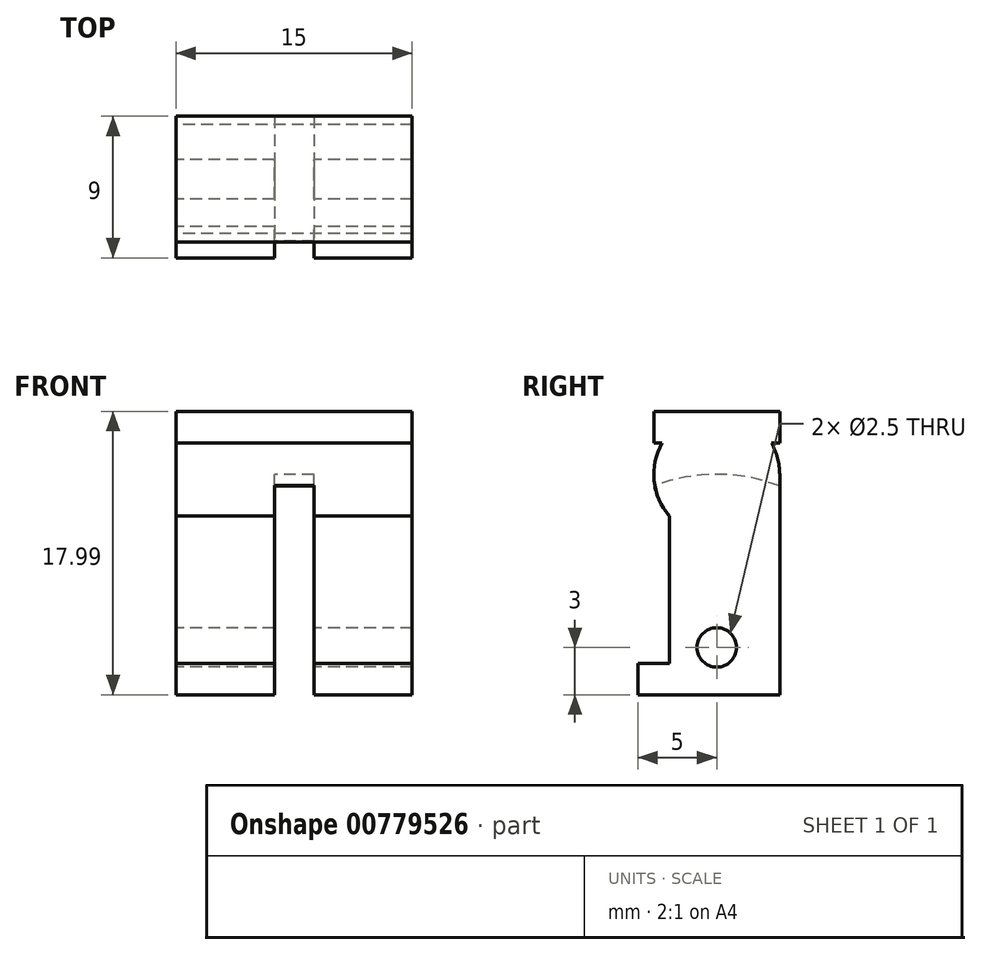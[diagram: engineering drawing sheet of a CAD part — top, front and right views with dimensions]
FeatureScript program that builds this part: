
annotation { "Feature Type Name" : "Feature", "Feature Type Description" : "" }
export const myFeature = defineFeature(function(context is Context, id is Id, definition is map)
    precondition{}
    {
        {
            var Q0;
            Q0=qCreatedBy(makeId("Right.planeOp"),FACE);
            var sketch = newSketch(context, id + "F0", { "sketchPlane" : qUnion([Q0])});
            skLineSegment(sketch, "E0.bottom", {"start": v(4, -1) * mm, "end": v(3.46, -1) * mm});
            skLineSegment(sketch, "E0.top", {"start": v(4, 1) * mm, "end": v(-4, 1) * mm});
            skLineSegment(sketch, "E0.left", {"start": v(4, -1) * mm, "end": v(4, 1) * mm});
            skLineSegment(sketch, "E0.right", {"start": v(-4, -1) * mm, "end": v(-4, 1) * mm});
            skPoint(sketch, "E0.middle", {"position": v(0, 0) * mm});
            skArc(sketch, "E1", {"start": v(-3.46, -1) * mm, "mid": v(-3.98, -3.4) * mm, "end": v(-3, -5.65) * mm});
            skLineSegment(sketch, "E2.left", {"start": v(4, -3) * mm, "end": v(4, -15) * mm});
            skLineSegment(sketch, "E2.right", {"start": v(-3, -5.65) * mm, "end": v(-3, -15) * mm});
            skLineSegment(sketch, "E3.top", {"start": v(4, -17) * mm, "end": v(-5, -17) * mm});
            skLineSegment(sketch, "E3.left", {"start": v(4, -15) * mm, "end": v(4, -17) * mm});
            skLineSegment(sketch, "E3.right", {"start": v(-5, -15) * mm, "end": v(-5, -17) * mm});
            skCircle(sketch, "E4", {"center": v(0, -14) * mm, "radius": 1.25 * mm});
            skLineSegment(sketch, "E5.trimOffspring", {"start": v(-3.46, -1) * mm, "end": v(-4, -1) * mm});
            skArc(sketch, "E6.trimOffspring", {"start": v(4, -3) * mm, "mid": v(3.86, -1.96) * mm, "end": v(3.46, -1) * mm});
            skLineSegment(sketch, "E7.trimOffspring", {"start": v(-3, -15) * mm, "end": v(-5, -15) * mm});
            skSolve(sketch);
        }
        {
            var Q0;
            Q0 = qSketchRegion(id + "F0", true);
            extrude(context, id + "F1", {"entities" : qUnion([Q0]), "endBound" : BoundingType.SYMMETRIC, "depth" : 15 * mm, "offsetDistance" : 25 * mm});
        }
        {
            var Q0;
            Q0=qCreatedBy(makeId("Right.planeOp"),FACE);
            var sketch = newSketch(context, id + "F2", { "sketchPlane" : qUnion([Q0])});
            skCircle(sketch, "E8", {"center": v(0, -14) * mm, "radius": 11 * mm});
            skSolve(sketch);
        }
        {
            var Q0;
            Q0 = qSketchRegion(id + "F2", true);
            extrude(context, id + "F3", {"entities" : qUnion([Q0]), "operationType" : NewBodyOperationType.REMOVE, "endBound" : BoundingType.SYMMETRIC, "depth" : 2.5 * mm, "offsetDistance" : 25 * mm});
        }
    });
